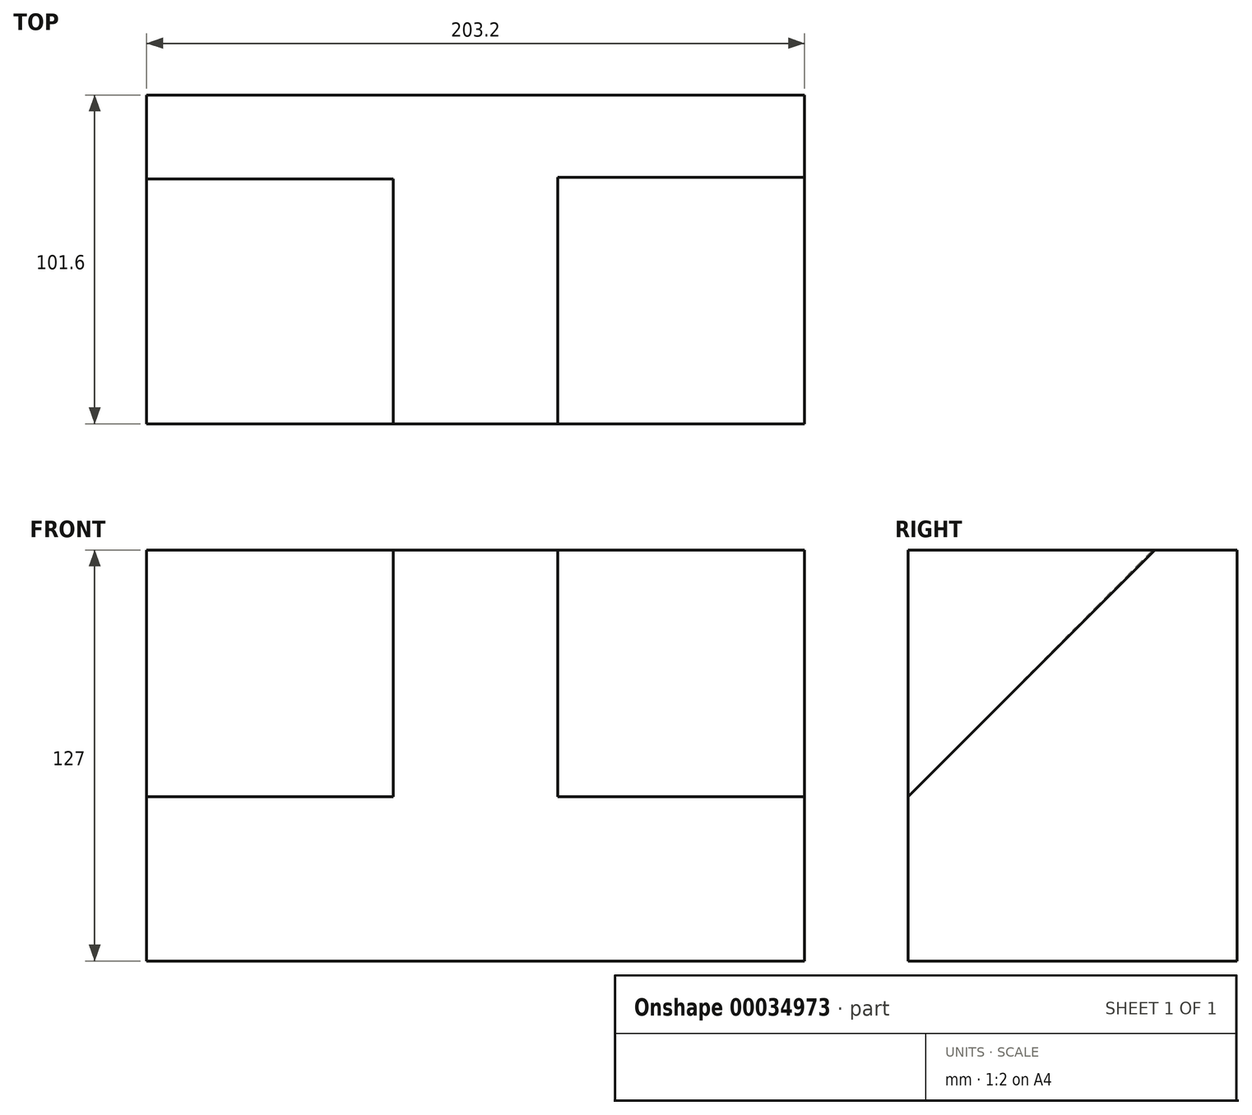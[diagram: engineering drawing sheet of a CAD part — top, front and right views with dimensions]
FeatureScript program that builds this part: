
annotation { "Feature Type Name" : "Feature", "Feature Type Description" : "" }
export const myFeature = defineFeature(function(context is Context, id is Id, definition is map)
    precondition{}
    {
        {
            var Q0;
            Q0=qCreatedBy(makeId("Top.planeOp"),FACE);
            var sketch = newSketch(context, id + "F4", { "sketchPlane" : qUnion([Q0])});
            skLineSegment(sketch, "E0.bottom", {"start": v(-56.11, 53.87) * mm, "end": v(147.09, 53.87) * mm});
            skLineSegment(sketch, "E0.top", {"start": v(-56.11, -47.73) * mm, "end": v(147.09, -47.73) * mm});
            skLineSegment(sketch, "E0.left", {"start": v(-56.11, 53.87) * mm, "end": v(-56.11, -47.73) * mm});
            skLineSegment(sketch, "E0.right", {"start": v(147.09, 53.87) * mm, "end": v(147.09, -47.73) * mm});
            skSolve(sketch);
        }
        {
            var Q0;
            Q0 = qSketchRegion(id + "F4", true);
            var Q1;
            Q1=makeQuery(id+"F4.imprint","IMPRINT",FACE,{"disambiguationData":[TD([[makeQuery(id+"F4.imprint","IMPRINT",EDGE,{"derivedFrom":sQuery(id+"F4.wireOp",EDGE,"E0.bottom")}),-1.0]])]});
            extrude(context, id + "F5", {"entities" : qUnion([Q0, Q1]), "depth" : 127 * mm});
        }
        {
            var Q0;
            Q0=makeQuery(id+"F5.opExtrude","SWEPT_FACE",FACE,{"disambiguationData":[OSD([sQuery(id+"F4.wireOp",EDGE,"E0.right")])]});
            var sketch = newSketch(context, id + "F0", { "sketchPlane" : qUnion([Q0])});
            skLineSegment(sketch, "E1", {"start": v(53.87, 127) * mm, "end": v(28.47, 127) * mm});
            skLineSegment(sketch, "E2", {"start": v(-47.73, 0) * mm, "end": v(-47.73, 50.8) * mm});
            skLineSegment(sketch, "E3", {"start": v(-47.73, 50.8) * mm, "end": v(28.47, 127) * mm});
            skSolve(sketch);
        }
        {
            var Q0;
            Q0 = qSketchRegion(id + "F0", true);
            var Q1;
            {var subQ2=sQuery(id+"F0.wireOp",EDGE,"E3");Q1=makeQuery(id+"F0.imprint","IMPRINT",FACE,{"disambiguationData":[TD([[makeQuery(id+"F0.imprint","IMPRINT",EDGE,{"derivedFrom":subQ2}),1.0]])]});}
            extrude(context, id + "F1", {"entities" : qUnion([Q0, Q1]), "operationType" : NewBodyOperationType.REMOVE, "oppositeDirection" : true, "depth" : 76.2 * mm});
        }
        {
            var Q0;
            Q0=makeQuery(id+"F5.opExtrude","SWEPT_FACE",FACE,{"disambiguationData":[OSD([sQuery(id+"F4.wireOp",EDGE,"E0.left")])]});
            var sketch = newSketch(context, id + "F2", { "sketchPlane" : qUnion([Q0])});
            skLineSegment(sketch, "E4", {"start": v(-53.25, 127.34) * mm, "end": v(-27.85, 127.36) * mm});
            skLineSegment(sketch, "E5", {"start": v(47.73, 0) * mm, "end": v(47.73, 50.8) * mm});
            skLineSegment(sketch, "E6", {"start": v(-27.85, 127) * mm, "end": v(47.73, 50.8) * mm});
            skSolve(sketch);
        }
        {
            var Q0;
            {var subQ2=sQuery(id+"F2.wireOp",EDGE,"E6");Q0=makeQuery(id+"F2.imprint","IMPRINT",FACE,{"disambiguationData":[TD([[makeQuery(id+"F2.imprint","IMPRINT",EDGE,{"derivedFrom":subQ2}),1.0]])]});}
            extrude(context, id + "F3", {"entities" : qUnion([Q0]), "operationType" : NewBodyOperationType.REMOVE, "oppositeDirection" : true, "depth" : 76.2 * mm});
        }
    });
